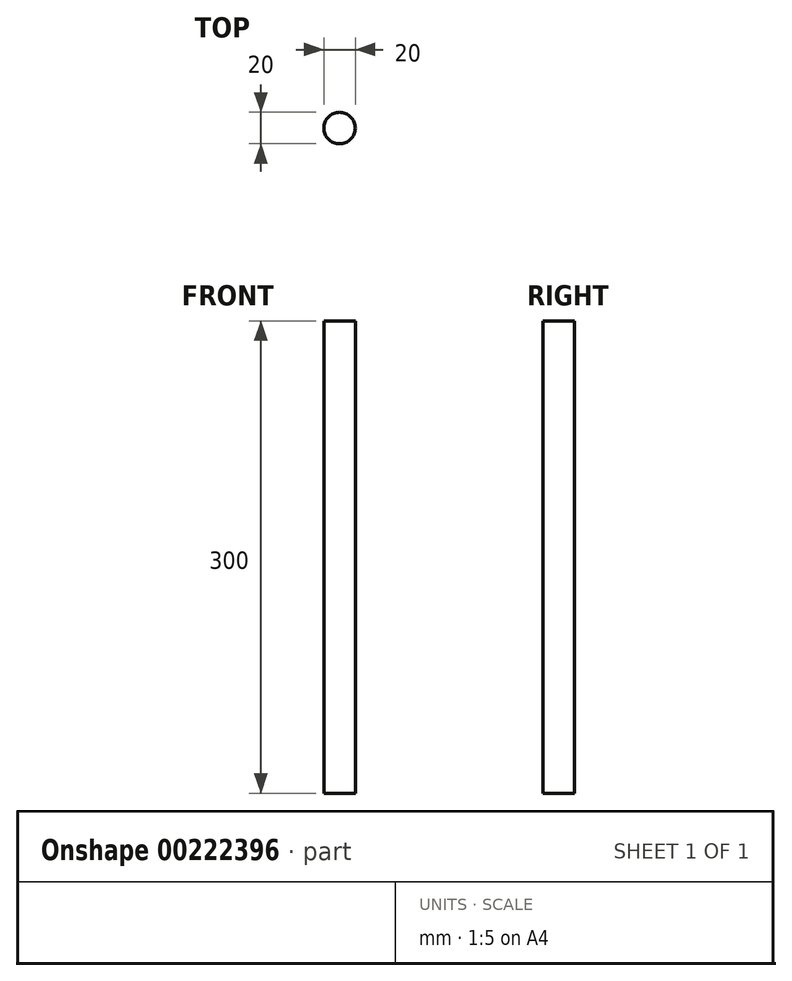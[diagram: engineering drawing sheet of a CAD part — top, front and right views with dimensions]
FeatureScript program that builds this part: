
annotation { "Feature Type Name" : "Feature", "Feature Type Description" : "" }
export const myFeature = defineFeature(function(context is Context, id is Id, definition is map)
    precondition{}
    {
        {
            var Q0;
            Q0=qCreatedBy(makeId("Top.planeOp"),FACE);
            var sketch = newSketch(context, id + "F0", { "sketchPlane" : qUnion([Q0])});
            skCircle(sketch, "E0", {"center": v(0, 0) * mm, "radius": 10 * mm});
            skSolve(sketch);
        }
        {
            var Q0;
            Q0=makeQuery(id+"F0.imprint","IMPRINT",FACE,{"disambiguationData":[TD([[makeQuery(id+"F0.imprint","IMPRINT",EDGE,{"derivedFrom":sQuery(id+"F0.wireOp",EDGE,"E0")}),1.0]])]});
            extrude(context, id + "F1", {"entities" : qUnion([Q0]), "endBound" : BoundingType.SYMMETRIC, "depth" : 300 * mm});
        }
    });
